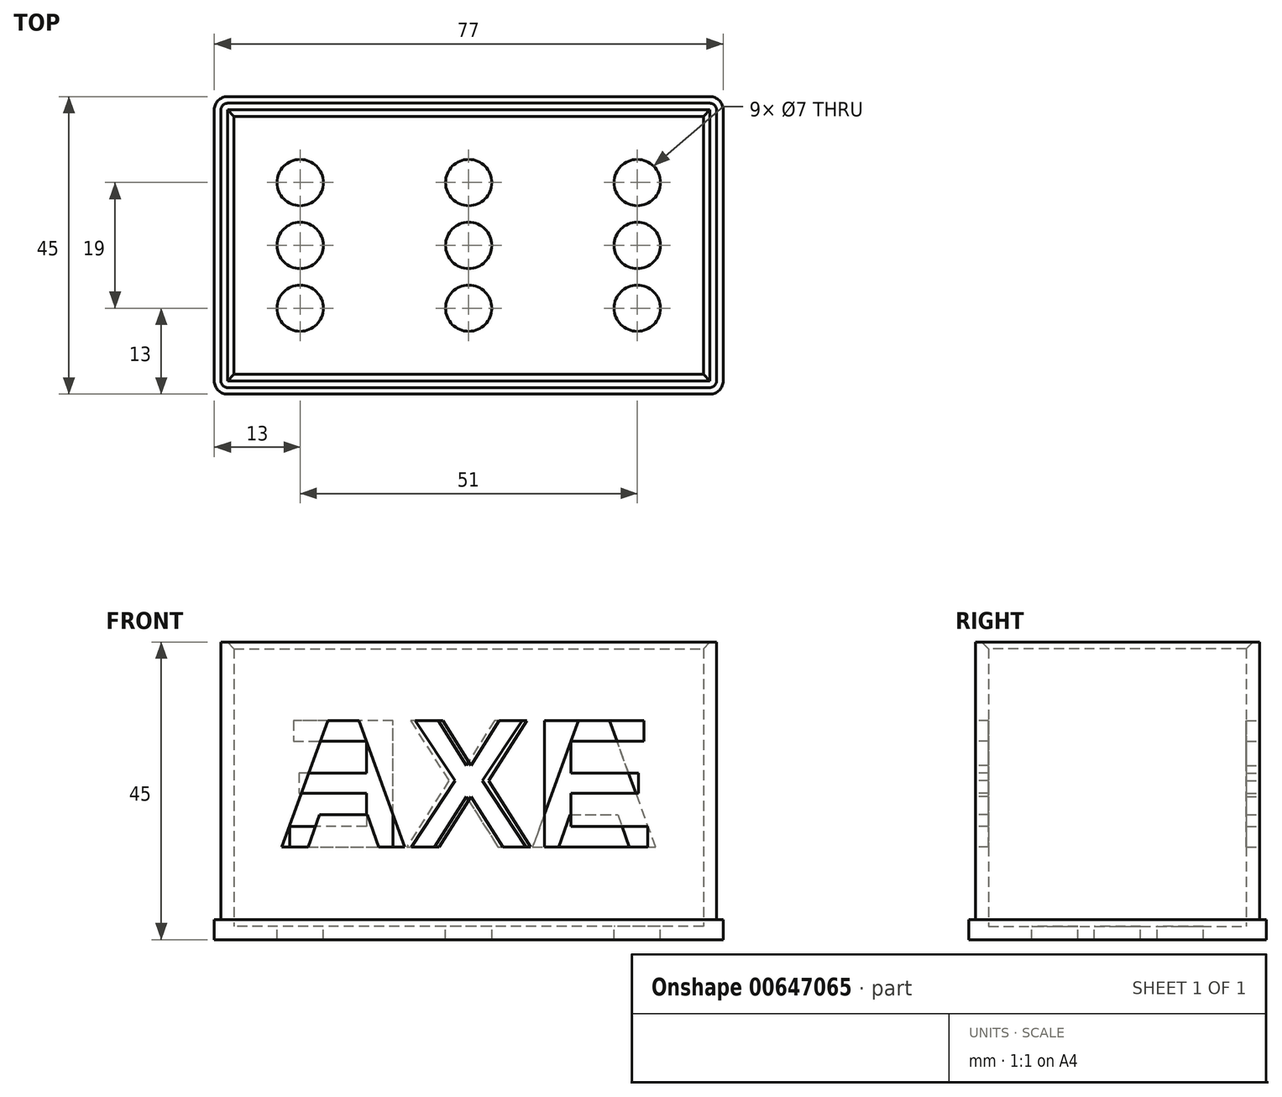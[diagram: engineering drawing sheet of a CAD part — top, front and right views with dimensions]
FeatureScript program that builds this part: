
annotation { "Feature Type Name" : "Feature", "Feature Type Description" : "" }
export const myFeature = defineFeature(function(context is Context, id is Id, definition is map)
    precondition{}
    {
        {
            var Q0;
            Q0=qCreatedBy(makeId("Top.planeOp"),FACE);
            var sketch = newSketch(context, id + "F0", { "sketchPlane" : qUnion([Q0])});
            skArc(sketch, "E0", {"start": v(-38.5, 22.5) * mm, "mid": v(-48.52, 0) * mm, "end": v(-38.5, -22.5) * mm});
            skLineSegment(sketch, "E1.bottom", {"start": v(-38.5, 22.5) * mm, "end": v(38.5, 22.5) * mm});
            skLineSegment(sketch, "E1.top", {"start": v(-38.5, -22.5) * mm, "end": v(38.5, -22.5) * mm});
            skLineSegment(sketch, "E1.left", {"start": v(-38.5, 22.5) * mm, "end": v(-38.5, -22.5) * mm});
            skLineSegment(sketch, "E1.right", {"start": v(38.5, 22.5) * mm, "end": v(38.5, -22.5) * mm});
            skSolve(sketch);
        }
        {
            var Q0;
            Q0 = qSketchRegion(id + "F0", true);
            extrude(context, id + "F1", {"entities" : qUnion([Q0]), "depth" : 3 * mm, "offsetDistance" : 25 * mm});
        }
        {
            var Q0;
            Q0=makeQuery(id+"F1.opExtrude","CAP_FACE",FACE,{"disambiguationData":[OSD([sQuery(id+"F0.wireOp",EDGE,"w9BDVdag-le7I-Owjt-72CQ-P1AIU4k5UJcO"),sQuery(id+"F0.wireOp",EDGE,"NQvOb2GB-TYaW-nJ4l-XIyY-iKGvsDs9XX0T"),sQuery(id+"F0.wireOp",EDGE,"hmEEFxGW-W0xg-Yi9A-DPnW-anLAEUFYmaK9"),sQuery(id+"F0.wireOp",EDGE,"E0")])],"isStart":false});
            var sketch = newSketch(context, id + "F2", { "sketchPlane" : qUnion([Q0])});
            skLineSegment(sketch, "E2.bottom", {"start": v(-37.5, 21.5) * mm, "end": v(37.5, 21.5) * mm});
            skLineSegment(sketch, "E2.top", {"start": v(-37.5, -21.5) * mm, "end": v(37.5, -21.5) * mm});
            skLineSegment(sketch, "E2.left", {"start": v(-37.5, 21.5) * mm, "end": v(-37.5, -21.5) * mm});
            skLineSegment(sketch, "E2.right", {"start": v(37.5, 21.5) * mm, "end": v(37.5, -21.5) * mm});
            skSolve(sketch);
        }
        {
            var Q0;
            Q0 = qSketchRegion(id + "F2", true);
            extrude(context, id + "F3", {"entities" : qUnion([Q0]), "operationType" : NewBodyOperationType.ADD, "depth" : 42 * mm, "offsetDistance" : 25 * mm});
        }
        {
            var Q0;
            Q0=makeQuery(id+"F3.opExtrude","CAP_FACE",FACE,{"disambiguationData":[OSD([sQuery(id+"F2.wireOp",EDGE,"E2.bottom"),sQuery(id+"F2.wireOp",EDGE,"E2.top"),sQuery(id+"F2.wireOp",EDGE,"E2.left"),sQuery(id+"F2.wireOp",EDGE,"E2.right")])],"isStart":false});
            shell(context, id + "F4", {"entities" : qUnion([Q0]), "thickness" : 2 * mm});
        }
        {
            var Q0;
            Q0=makeQuery(id+"F4.opShell","OFFSET_FACE",FACE,{"disambiguationData":[OSD([sQuery(id+"F0.wireOp",EDGE,"w9BDVdag-le7I-Owjt-72CQ-P1AIU4k5UJcO"),sQuery(id+"F0.wireOp",EDGE,"NQvOb2GB-TYaW-nJ4l-XIyY-iKGvsDs9XX0T"),sQuery(id+"F0.wireOp",EDGE,"hmEEFxGW-W0xg-Yi9A-DPnW-anLAEUFYmaK9"),sQuery(id+"F0.wireOp",EDGE,"E0")])]});
            var sketch = newSketch(context, id + "F5", { "sketchPlane" : qUnion([Q0])});
            skLineSegment(sketch, "E3.bottom", {"start": v(-25.5, 9.5) * mm, "end": v(25.5, 9.5) * mm});
            skLineSegment(sketch, "E3.top", {"start": v(-25.5, -9.5) * mm, "end": v(25.5, -9.5) * mm});
            skLineSegment(sketch, "E3.left", {"start": v(-25.5, 9.5) * mm, "end": v(-25.5, -9.5) * mm});
            skLineSegment(sketch, "E3.right", {"start": v(25.5, 9.5) * mm, "end": v(25.5, -9.5) * mm});
            skPoint(sketch, "E4", {"position": v(-25.5, 9.5) * mm});
            skPoint(sketch, "E5", {"position": v(0, 9.5) * mm});
            skPoint(sketch, "E6", {"position": v(25.5, 9.5) * mm});
            skPoint(sketch, "E7", {"position": v(25.5, -9.5) * mm});
            skPoint(sketch, "E8", {"position": v(0, -9.5) * mm});
            skPoint(sketch, "E9", {"position": v(-25.5, -9.5) * mm});
            skPoint(sketch, "E10", {"position": v(0, 0) * mm});
            skPoint(sketch, "E11", {"position": v(-25.5, 0) * mm});
            skPoint(sketch, "E12", {"position": v(25.5, 0) * mm});
            skSolve(sketch);
        }
        {
            var Q0;
            Q0=sQuery(id+"F5.wireOp",VERTEX,"E4");
            var Q1;
            Q1=sQuery(id+"F5.wireOp",VERTEX,"E5");
            var Q2;
            Q2=sQuery(id+"F5.wireOp",VERTEX,"E6");
            var Q3;
            Q3=sQuery(id+"F5.wireOp",VERTEX,"E10");
            var Q4;
            Q4=sQuery(id+"F5.wireOp",VERTEX,"E11");
            var Q5;
            Q5=sQuery(id+"F5.wireOp",VERTEX,"E9");
            var Q6;
            Q6=sQuery(id+"F5.wireOp",VERTEX,"E8");
            var Q7;
            Q7=sQuery(id+"F5.wireOp",VERTEX,"E7");
            var Q8;
            Q8=sQuery(id+"F5.wireOp",VERTEX,"E12");
            var Q9;
            Q9=makeQuery(id+"F1.opExtrude","SWEPT_BODY",BODY,{"disambiguationData":[OSD([sQuery(id+"F0.wireOp",EDGE,"w9BDVdag-le7I-Owjt-72CQ-P1AIU4k5UJcO"),sQuery(id+"F0.wireOp",EDGE,"NQvOb2GB-TYaW-nJ4l-XIyY-iKGvsDs9XX0T"),sQuery(id+"F0.wireOp",EDGE,"hmEEFxGW-W0xg-Yi9A-DPnW-anLAEUFYmaK9"),sQuery(id+"F0.wireOp",EDGE,"E0")])]});
            hole(context, id + "F6", {"style" : HoleStyle.SIMPLE, "endStyle" : HoleEndStyle.BLIND, "holeDiameter" : 7 * mm, "majorDiameter" : 5 * mm, "holeDepth" : 15 * mm, "isTappedThrough" : true, "tappedDepth" : 12 * mm, "tapClearance" : 3, "startFromSketch" : true, "locations" : qUnion([Q0, Q1, Q2, Q3, Q4, Q5, Q6, Q7, Q8]), "scope" : qUnion([Q9])});
        }
        {
            var Q0;
            Q0=makeQuery(id+"F4.opShell","OFFSET_EDGE",EDGE,{"disambiguationData":[OSD([sQuery(id+"F2.wireOp",EDGE,"E2.top")])]});
            var Q1;
            Q1=makeQuery(id+"F4.opShell","OFFSET_EDGE",EDGE,{"disambiguationData":[OSD([sQuery(id+"F2.wireOp",EDGE,"E2.left")])]});
            var Q2;
            Q2=makeQuery(id+"F4.opShell","OFFSET_EDGE",EDGE,{"disambiguationData":[OSD([sQuery(id+"F2.wireOp",EDGE,"E2.bottom")])]});
            var Q3;
            Q3=makeQuery(id+"F4.opShell","OFFSET_EDGE",EDGE,{"disambiguationData":[OSD([sQuery(id+"F2.wireOp",EDGE,"E2.right")])]});
            var Q4;
            Q4=makeQuery(id+"F6.hole-0.boolean.opBoolean","COPY",EDGE,{"derivedFrom":makeQuery(id+"F6.hole-0.opRevolve","SWEPT_EDGE",EDGE,{"disambiguationData":[OSD([sQuery(id+"F6.hole-0.sketch.wireOp",EDGE,"core_line_2"),sQuery(id+"F6.hole-0.sketch.wireOp",EDGE,"core_line_3")])]})});
            var Q5;
            Q5=makeQuery(id+"F6.hole-4.boolean.opBoolean","COPY",EDGE,{"derivedFrom":makeQuery(id+"F6.hole-4.opRevolve","SWEPT_EDGE",EDGE,{"disambiguationData":[OSD([sQuery(id+"F6.hole-4.sketch.wireOp",EDGE,"core_line_2"),sQuery(id+"F6.hole-4.sketch.wireOp",EDGE,"core_line_3")])]})});
            var Q6;
            Q6=makeQuery(id+"F6.hole-5.boolean.opBoolean","COPY",EDGE,{"derivedFrom":makeQuery(id+"F6.hole-5.opRevolve","SWEPT_EDGE",EDGE,{"disambiguationData":[OSD([sQuery(id+"F6.hole-5.sketch.wireOp",EDGE,"core_line_2"),sQuery(id+"F6.hole-5.sketch.wireOp",EDGE,"core_line_3")])]})});
            var Q7;
            Q7=makeQuery(id+"F6.hole-1.boolean.opBoolean","COPY",EDGE,{"derivedFrom":makeQuery(id+"F6.hole-1.opRevolve","SWEPT_EDGE",EDGE,{"disambiguationData":[OSD([sQuery(id+"F6.hole-1.sketch.wireOp",EDGE,"core_line_2"),sQuery(id+"F6.hole-1.sketch.wireOp",EDGE,"core_line_3")])]})});
            var Q8;
            Q8=makeQuery(id+"F6.hole-3.boolean.opBoolean","COPY",EDGE,{"derivedFrom":makeQuery(id+"F6.hole-3.opRevolve","SWEPT_EDGE",EDGE,{"disambiguationData":[OSD([sQuery(id+"F6.hole-3.sketch.wireOp",EDGE,"core_line_2"),sQuery(id+"F6.hole-3.sketch.wireOp",EDGE,"core_line_3")])]})});
            var Q9;
            Q9=makeQuery(id+"F6.hole-6.boolean.opBoolean","COPY",EDGE,{"derivedFrom":makeQuery(id+"F6.hole-6.opRevolve","SWEPT_EDGE",EDGE,{"disambiguationData":[OSD([sQuery(id+"F6.hole-6.sketch.wireOp",EDGE,"core_line_2"),sQuery(id+"F6.hole-6.sketch.wireOp",EDGE,"core_line_3")])]})});
            var Q10;
            Q10=makeQuery(id+"F6.hole-7.boolean.opBoolean","COPY",EDGE,{"derivedFrom":makeQuery(id+"F6.hole-7.opRevolve","SWEPT_EDGE",EDGE,{"disambiguationData":[OSD([sQuery(id+"F6.hole-7.sketch.wireOp",EDGE,"core_line_2"),sQuery(id+"F6.hole-7.sketch.wireOp",EDGE,"core_line_3")])]})});
            var Q11;
            Q11=makeQuery(id+"F6.hole-8.boolean.opBoolean","COPY",EDGE,{"derivedFrom":makeQuery(id+"F6.hole-8.opRevolve","SWEPT_EDGE",EDGE,{"disambiguationData":[OSD([sQuery(id+"F6.hole-8.sketch.wireOp",EDGE,"core_line_2"),sQuery(id+"F6.hole-8.sketch.wireOp",EDGE,"core_line_3")])]})});
            var Q12;
            Q12=makeQuery(id+"F6.hole-2.boolean.opBoolean","COPY",EDGE,{"derivedFrom":makeQuery(id+"F6.hole-2.opRevolve","SWEPT_EDGE",EDGE,{"disambiguationData":[OSD([sQuery(id+"F6.hole-2.sketch.wireOp",EDGE,"core_line_2"),sQuery(id+"F6.hole-2.sketch.wireOp",EDGE,"core_line_3")])]})});
            chamfer(context, id + "F7", {"entities" : qUnion([Q0, Q1, Q2, Q3, Q4, Q5, Q6, Q7, Q8, Q9, Q10, Q11, Q12]), "width" : 1 * mm, "tangentPropagation" : true});
        }
        {
            var Q0;
            Q0=makeQuery(id+"F3.opExtrude","SWEPT_EDGE",EDGE,{"disambiguationData":[OSD([sQuery(id+"F2.wireOp",EDGE,"E2.bottom"),sQuery(id+"F2.wireOp",EDGE,"E2.right")])]});
            var Q1;
            Q1=makeQuery(id+"F3.opExtrude","SWEPT_EDGE",EDGE,{"disambiguationData":[OSD([sQuery(id+"F2.wireOp",EDGE,"E2.top"),sQuery(id+"F2.wireOp",EDGE,"E2.right")])]});
            var Q2;
            Q2=makeQuery(id+"F3.opExtrude","SWEPT_EDGE",EDGE,{"disambiguationData":[OSD([sQuery(id+"F2.wireOp",EDGE,"E2.top"),sQuery(id+"F2.wireOp",EDGE,"E2.left")])]});
            var Q3;
            Q3=makeQuery(id+"F3.opExtrude","SWEPT_EDGE",EDGE,{"disambiguationData":[OSD([sQuery(id+"F2.wireOp",EDGE,"E2.bottom"),sQuery(id+"F2.wireOp",EDGE,"E2.left")])]});
            fillet(context, id + "F8", {"entities" : qUnion([Q0, Q1, Q2, Q3]), "radius" : 1 * mm, "tangentPropagation" : true, "allowEdgeOverflow" : false});
        }
        {
            var Q0;
            Q0=makeQuery(id+"F3.opExtrude","SWEPT_FACE",FACE,{"disambiguationData":[OSD([sQuery(id+"F2.wireOp",EDGE,"E2.bottom")])]});
            var sketch = newSketch(context, id + "F9", { "sketchPlane" : qUnion([Q0])});
            skText(sketch, "E13", { "text": "AXE", "fontName": "Arimo-Bold.ttf"});
            const initialGuessF9  = {"E13": [-0.02898, 0.014, 1, 0, 0.02]};
            skSetInitialGuess(sketch, initialGuessF9);
            skSolve(sketch);
        }
        {
            var Q0;
            Q0 = qSketchRegion(id + "F9", true);
            var Q1;
            Q1=makeQuery(id+"F9.imprint","IMPRINT",FACE,{"disambiguationData":[TD([[makeQuery(id+"F9.imprint","IMPRINT",EDGE,{"derivedFrom":sQuery(id+"F9.wireOp",EDGE,"E13.sketch_text.stroke-8")}),1.0]])]});
            extrude(context, id + "F10", {"entities" : qUnion([Q0, Q1]), "operationType" : NewBodyOperationType.REMOVE, "oppositeDirection" : true, "depth" : 5 * mm, "offsetDistance" : 25 * mm});
        }
        {
            var Q0;
            Q0=makeQuery(id+"F3.opExtrude","SWEPT_FACE",FACE,{"disambiguationData":[OSD([sQuery(id+"F2.wireOp",EDGE,"E2.top")])]});
            var sketch = newSketch(context, id + "F11", { "sketchPlane" : qUnion([Q0])});
            skText(sketch, "E14", { "text": "AXE", "fontName": "Arimo-Bold.ttf"});
            const initialGuessF11  = {"E14": [-0.02898, 0.014, 1, 0, 0.02]};
            skSetInitialGuess(sketch, initialGuessF11);
            skSolve(sketch);
        }
        {
            var Q0;
            Q0=makeQuery(id+"F11.imprint","IMPRINT",FACE,{"disambiguationData":[TD([[makeQuery(id+"F11.imprint","IMPRINT",EDGE,{"derivedFrom":sQuery(id+"F11.wireOp",EDGE,"E14.sketch_text.stroke-8")}),1.0]])]});
            var Q1;
            Q1=makeQuery(id+"F11.imprint","IMPRINT",FACE,{"disambiguationData":[TD([[makeQuery(id+"F11.imprint","IMPRINT",EDGE,{"derivedFrom":sQuery(id+"F11.wireOp",EDGE,"E14.sketch_text.stroke-0")}),-1.0]])]});
            var Q2;
            Q2=makeQuery(id+"F11.imprint","IMPRINT",FACE,{"disambiguationData":[TD([[makeQuery(id+"F11.imprint","IMPRINT",EDGE,{"derivedFrom":sQuery(id+"F11.wireOp",EDGE,"E14.sketch_text.stroke-15")}),-1.0]])]});
            var Q3;
            Q3=makeQuery(id+"F11.imprint","IMPRINT",FACE,{"disambiguationData":[TD([[makeQuery(id+"F11.imprint","IMPRINT",EDGE,{"derivedFrom":sQuery(id+"F11.wireOp",EDGE,"E14.sketch_text.stroke-27")}),-1.0]])]});
            extrude(context, id + "F12", {"entities" : qUnion([Q0, Q1, Q2, Q3]), "operationType" : NewBodyOperationType.REMOVE, "oppositeDirection" : true, "depth" : 5 * mm, "offsetDistance" : 25 * mm});
        }
        {
            var Q0;
            Q0=makeQuery(id+"F0.imprint","IMPRINT",FACE,{"disambiguationData":[TD([[makeQuery(id+"F0.imprint","IMPRINT",EDGE,{"derivedFrom":sQuery(id+"F0.wireOp",EDGE,"E0")}),1.0]])]});
            extrude(context, id + "F13", {"entities" : qUnion([Q0]), "operationType" : NewBodyOperationType.REMOVE, "depth" : 25 * mm, "offsetDistance" : 25 * mm});
        }
        {
            var Q0;
            {var subQ0=sQuery(id+"F0.wireOp",EDGE,"E1.left");var subQ1=sQuery(id+"F0.wireOp",EDGE,"E1.bottom");var subQ2=sQuery(id+"F0.wireOp",EDGE,"E0");Q0=makeQuery(id+"F13.boolean.opBoolean","MERGE",EDGE,{"derivedFrom":[makeQuery(id+"F1.opExtrude","SWEPT_EDGE",EDGE,{"disambiguationData":[OSD([subQ2,subQ1,subQ0])]}),makeQuery(id+"F13.opExtrude","SWEPT_EDGE",EDGE,{"disambiguationData":[OSD([subQ2,subQ1,subQ0])]})]});}
            var Q1;
            {var subQ0=sQuery(id+"F0.wireOp",EDGE,"E1.left");var subQ1=sQuery(id+"F0.wireOp",EDGE,"E1.top");var subQ2=sQuery(id+"F0.wireOp",EDGE,"E0");Q1=makeQuery(id+"F13.boolean.opBoolean","MERGE",EDGE,{"derivedFrom":[makeQuery(id+"F1.opExtrude","SWEPT_EDGE",EDGE,{"disambiguationData":[OSD([subQ2,subQ1,subQ0])]}),makeQuery(id+"F13.opExtrude","SWEPT_EDGE",EDGE,{"disambiguationData":[OSD([subQ2,subQ1,subQ0])]})]});}
            var Q2;
            Q2=makeQuery(id+"F1.opExtrude","SWEPT_EDGE",EDGE,{"disambiguationData":[OSD([sQuery(id+"F0.wireOp",EDGE,"E1.top"),sQuery(id+"F0.wireOp",EDGE,"E1.right")])]});
            var Q3;
            Q3=makeQuery(id+"F1.opExtrude","SWEPT_EDGE",EDGE,{"disambiguationData":[OSD([sQuery(id+"F0.wireOp",EDGE,"E1.bottom"),sQuery(id+"F0.wireOp",EDGE,"E1.right")])]});
            fillet(context, id + "F14", {"entities" : qUnion([Q0, Q1, Q2, Q3]), "radius" : 2 * mm, "tangentPropagation" : true, "allowEdgeOverflow" : false});
        }
    });
